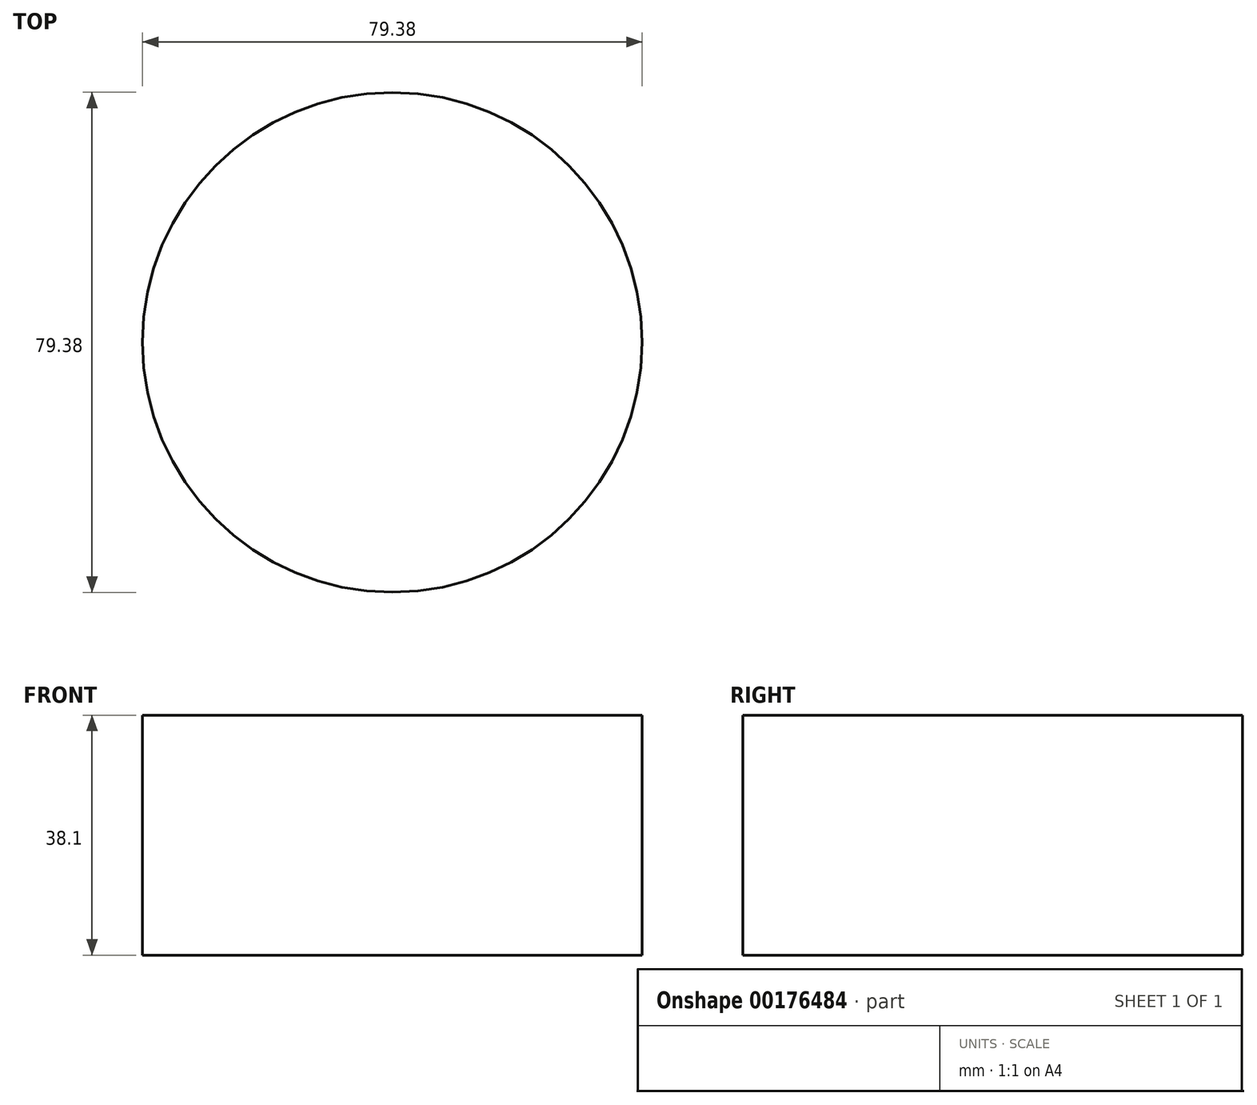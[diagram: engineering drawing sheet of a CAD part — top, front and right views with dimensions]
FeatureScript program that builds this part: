
annotation { "Feature Type Name" : "Feature", "Feature Type Description" : "" }
export const myFeature = defineFeature(function(context is Context, id is Id, definition is map)
    precondition{}
    {
        {
            var Q0;
            Q0=qCreatedBy(makeId("Top.planeOp"),FACE);
            var sketch = newSketch(context, id + "F0", { "sketchPlane" : qUnion([Q0])});
            skCircle(sketch, "E0", {"center": v(0, 0) * mm, "radius": 39.69 * mm});
            skSolve(sketch);
        }
        {
            var Q0;
            Q0=makeQuery(id+"F0.imprint","IMPRINT",FACE,{"disambiguationData":[TD([[makeQuery(id+"F0.imprint","IMPRINT",EDGE,{"derivedFrom":sQuery(id+"F0.wireOp",EDGE,"E0")}),1.0]])]});
            extrude(context, id + "F1", {"entities" : qUnion([Q0]), "depth" : 38.1 * mm});
        }
    });
